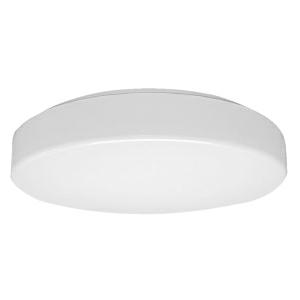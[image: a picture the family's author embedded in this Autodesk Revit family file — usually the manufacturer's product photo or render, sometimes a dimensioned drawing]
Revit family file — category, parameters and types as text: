
# Revit family: oblo_fit_-_oba_4000_840_d_00813355_8e14
name_source: partatom
category: Lighting Fixtures
units: mm (PartAtom-declared; Revit-internal decimal feet)

## family parameters
Cut with Voids When Loaded = No
Host = Face
Light Source = No
Part Type = Normal
Room Calculation Point = No
Round Connector Dimension = Use Diameter
Shared = No

## types (1)
- deko (1 x LED, 3350 lm, 4000K)
    Apparent Load = 44 VA
    Approval mark = CE
    CIE Flux Codes = 47 78 95 100 100
    Color Rendering = 80-89
    Color Temperature = 4000K
    Control Gear = Electronic ballast
    Default Elevation = 1800 mm
    Description = OBA 4000/840/D|Surface-mounted luminaire.|light source:   Cold white   |work equipment: Power supply unit|luminous flux: 4300 lm|light distribution: Direct|class of protection: I|technology: Continuously dimmable|mains lead: Direct power supply|glare control: without|special features: DALI Load 1x|
    Frequency = 50 Hz, 60 Hz
    Height = 95 mm
    Lamp = 1 x LED
    Lamp Light Flux = 3350 lm
    Lamp count = 1
    Length = 460 mm
    Luminous efficacy = 76 lm/W
    Manufacturer = Waldmann
    ModVariant = No
    Model = 00813355
    Mounting Place = Ceiling
    Mounting Type = Surface mounted
    Number of Poles = 1
    OnlyDefault = Yes
    Power Factor = 1
    Product Name = OBLO.fit - OBA 4000/840/D
    Product group = Ceiling mounted luminaire
    ProductGroupID = 3
    Protection Class = Protection class I
    Protection Degree = IP 40
    RLX_Detail_Level = 1
    RLX_Emergency_Light_Flux = 0 lm
    RLX_Emergency_Type = 0
    RLX_Emergency_Type_DB = No
    RlxData = <blob elided: 23705 chars, md5=bec4db0a>
    Socket = socket
    Standby Power = 0 W
    System Light Flux = 3350 lm
    System Power = 44 W
    Type Comments = mit Deko-Ring
    Type Image = oblo_led.jpg
    URL = http://relux.com
    VarID = deko
    Voltage = 230 V
    Voltage Range = 220-240 V
    Weight = 0.00 kg
    Width = 0 mm  [stored 0 ft]

note: [stored X ft] marks values corroborated as IEEE doubles in the binary element streams (Revit-internal decimal feet)

## geometry (parser evidence)
native form markers: Blend x4, Sweep x9
no freeform markers — native parametric forms only
